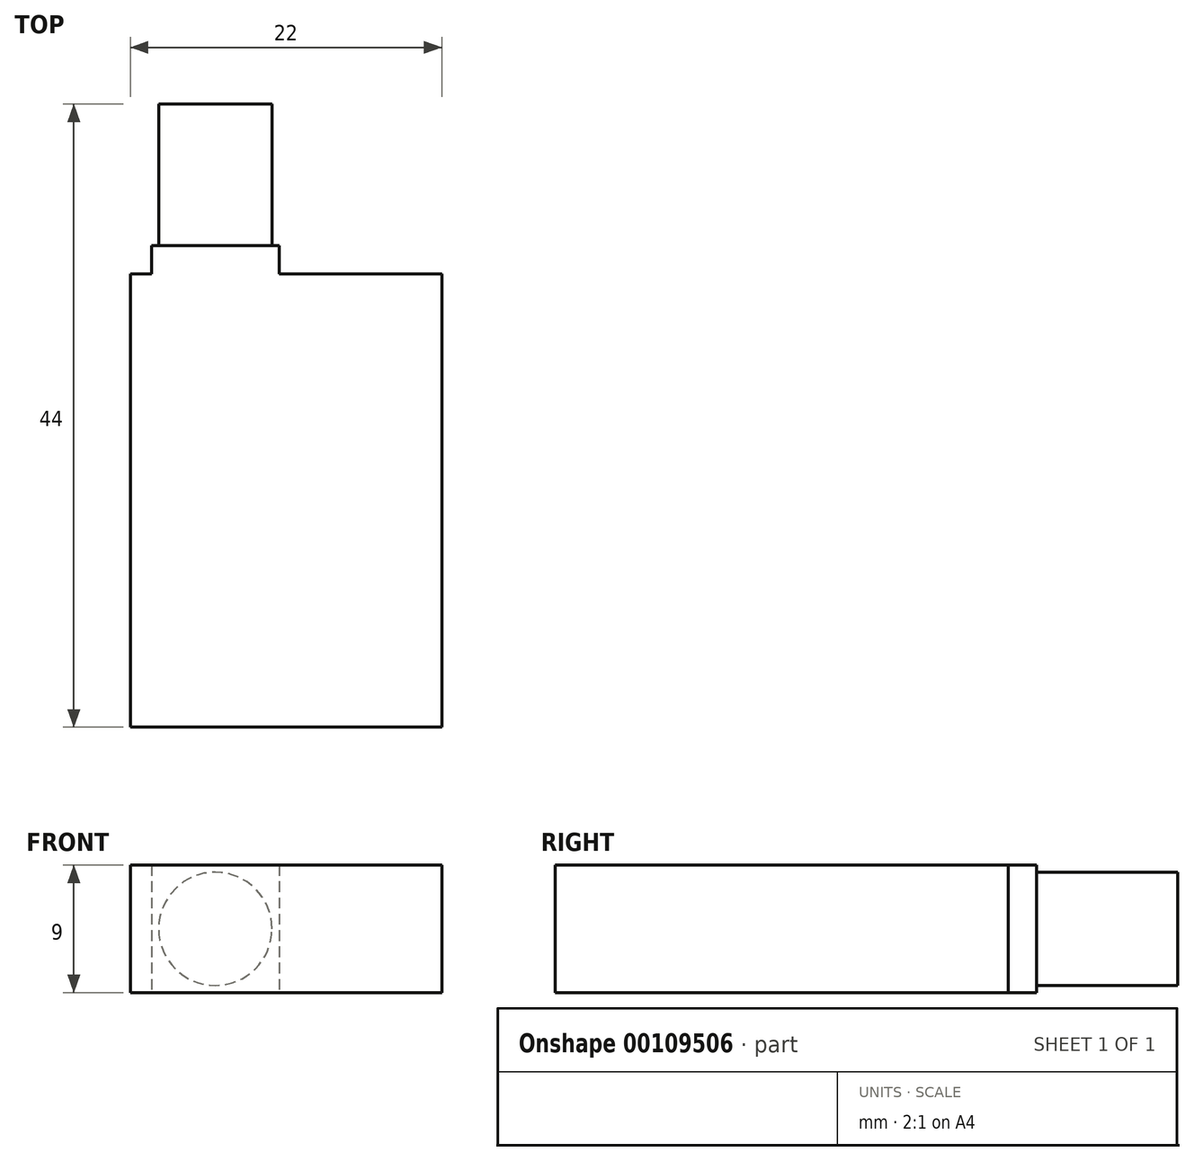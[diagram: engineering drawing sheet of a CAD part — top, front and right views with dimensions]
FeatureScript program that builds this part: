
annotation { "Feature Type Name" : "Feature", "Feature Type Description" : "" }
export const myFeature = defineFeature(function(context is Context, id is Id, definition is map)
    precondition{}
    {
        {
            var Q0;
            Q0=qCreatedBy(makeId("Top.planeOp"),FACE);
            var sketch = newSketch(context, id + "F0", { "sketchPlane" : qUnion([Q0])});
            skLineSegment(sketch, "E0.bottom", {"start": v(0, 0) * mm, "end": v(22, 0) * mm});
            skLineSegment(sketch, "E0.top", {"start": v(0, 32) * mm, "end": v(22, 32) * mm});
            skLineSegment(sketch, "E0.left", {"start": v(0, 0) * mm, "end": v(0, 32) * mm});
            skLineSegment(sketch, "E0.right", {"start": v(22, 0) * mm, "end": v(22, 32) * mm});
            skSolve(sketch);
        }
        {
            var Q0;
            Q0=qSketchRegion(id+"F0",true);
            extrude(context, id + "F1", {"entities" : qUnion([Q0]), "depth" : 9 * mm});
        }
        {
            var Q0;
            Q0=makeQuery(id+"F1.opExtrude","SWEPT_FACE",FACE,{"disambiguationData":[OSD([sQuery(id+"F0.wireOp",EDGE,"E0.top")])]});
            var sketch = newSketch(context, id + "F2", { "sketchPlane" : qUnion([Q0])});
            skLineSegment(sketch, "E1.bottom", {"start": v(-1.5, 9) * mm, "end": v(-10.5, 9) * mm});
            skLineSegment(sketch, "E1.top", {"start": v(-1.5, 0) * mm, "end": v(-10.5, 0) * mm});
            skLineSegment(sketch, "E1.left", {"start": v(-1.5, 9) * mm, "end": v(-1.5, 0) * mm});
            skLineSegment(sketch, "E1.right", {"start": v(-10.5, 9) * mm, "end": v(-10.5, 0) * mm});
            skSolve(sketch);
        }
        {
            var Q0;
            Q0=qSketchRegion(id+"F2",true);
            extrude(context, id + "F3", {"entities" : qUnion([Q0]), "operationType" : NewBodyOperationType.ADD, "depth" : 2 * mm});
        }
        {
            var Q0;
            Q0=makeQuery(id+"F3.opExtrude","CAP_FACE",FACE,{"disambiguationData":[OSD([sQuery(id+"F2.wireOp",EDGE,"E1.bottom"),sQuery(id+"F2.wireOp",EDGE,"E1.top"),sQuery(id+"F2.wireOp",EDGE,"E1.left"),sQuery(id+"F2.wireOp",EDGE,"E1.right")])],"isStart":false});
            var sketch = newSketch(context, id + "F4", { "sketchPlane" : qUnion([Q0])});
            skCircle(sketch, "E2", {"center": v(-6, 4.5) * mm, "radius": 4 * mm});
            skSolve(sketch);
        }
        {
            var Q0;
            Q0=qSketchRegion(id+"F4",true);
            extrude(context, id + "F5", {"entities" : qUnion([Q0]), "operationType" : NewBodyOperationType.ADD, "depth" : 10 * mm});
        }
    });
